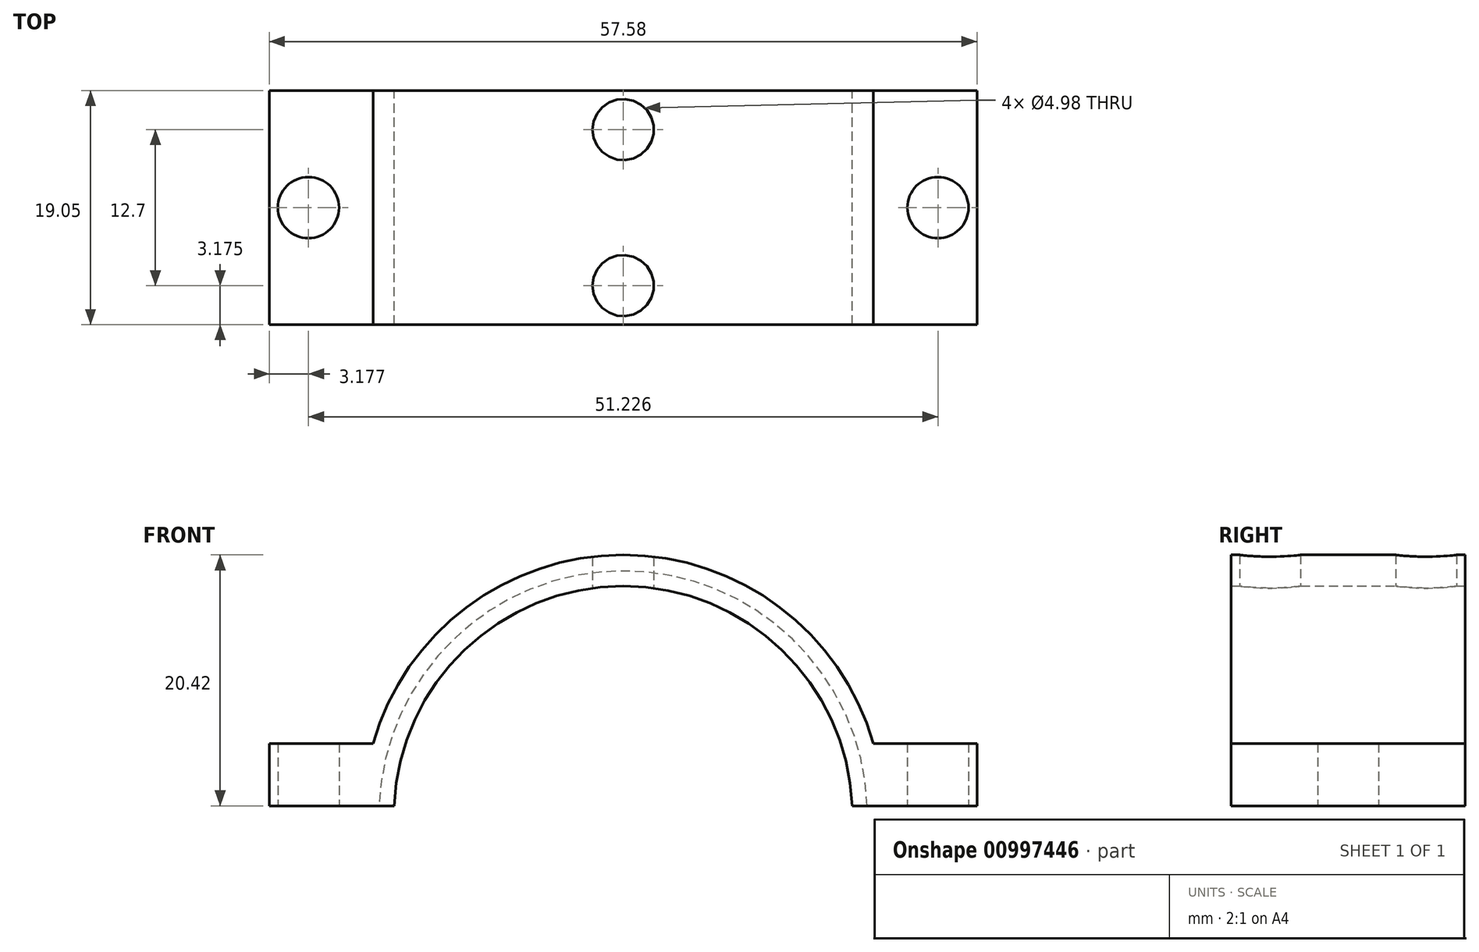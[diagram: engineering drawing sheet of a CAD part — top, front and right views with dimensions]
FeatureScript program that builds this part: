
annotation { "Feature Type Name" : "Feature", "Feature Type Description" : "" }
export const myFeature = defineFeature(function(context is Context, id is Id, definition is map)
    precondition{}
    {
        {
            var Q0;
            Q0=qCreatedBy(makeId("Front.planeOp"),FACE);
            var sketch = newSketch(context, id + "F0", { "sketchPlane" : qUnion([Q0])});
            skLineSegment(sketch, "E0", {"start": v(18.63, 0.76) * mm, "end": v(28.79, 0.76) * mm});
            skLineSegment(sketch, "E1", {"start": v(28.79, 0.76) * mm, "end": v(28.79, 5.84) * mm});
            skLineSegment(sketch, "E2", {"start": v(28.79, 5.84) * mm, "end": v(20.36, 5.84) * mm});
            skArc(sketch, "E3", {"start": v(18.63, 0.76) * mm, "mid": v(12.91, 13.45) * mm, "end": v(0, 18.64) * mm});
            skArc(sketch, "E4", {"start": v(20.36, 5.84) * mm, "mid": v(12.75, 16.92) * mm, "end": v(0, 21.18) * mm});
            skLineSegment(sketch, "E5", {"start": v(0, 21.18) * mm, "end": v(0, 18.64) * mm});
            skSolve(sketch);
        }
        {
            var Q0;
            Q0=makeQuery(id+"F0.imprint","IMPRINT",FACE,{"disambiguationData":[TD([[makeQuery(id+"F0.imprint","IMPRINT",EDGE,{"derivedFrom":sQuery(id+"F0.wireOp",EDGE,"E0")}),1.0]])]});
            extrude(context, id + "F1", {"entities" : qUnion([Q0]), "depth" : 19.05 * mm, "offsetDistance" : 25.4 * mm});
        }
        {
            var Q0;
            Q0=makeQuery(id+"F1.opExtrude","CAP_FACE",FACE,{"disambiguationData":[OSD([sQuery(id+"F0.wireOp",EDGE,"E0"),sQuery(id+"F0.wireOp",EDGE,"E1"),sQuery(id+"F0.wireOp",EDGE,"E2"),sQuery(id+"F0.wireOp",EDGE,"E3"),sQuery(id+"F0.wireOp",EDGE,"E4"),sQuery(id+"F0.wireOp",EDGE,"E5")])],"isStart":true});
            var sketch = newSketch(context, id + "F2", { "sketchPlane" : qUnion([Q0])});
            skArc(sketch, "E6", {"start": v(-19.88, 0) * mm, "mid": v(-14.05, 14.05) * mm, "end": v(0, 19.88) * mm});
            skLineSegment(sketch, "E7", {"start": v(0, 19.88) * mm, "end": v(0, 0) * mm});
            skLineSegment(sketch, "E8", {"start": v(0, 0) * mm, "end": v(-19.88, 0) * mm});
            skSolve(sketch);
        }
        {
            var Q0;
            Q0 = qSketchRegion(id + "F2", true);
            extrude(context, id + "F3", {"entities" : qUnion([Q0]), "operationType" : NewBodyOperationType.REMOVE, "oppositeDirection" : true, "depth" : 3 / 203.2 * mm, "offsetDistance" : 25.4 * mm});
        }
        {
            var Q0;
            Q0=makeQuery(id+"F1.opExtrude","SWEPT_BODY",BODY,{"disambiguationData":[OSD([sQuery(id+"F0.wireOp",EDGE,"E0"),sQuery(id+"F0.wireOp",EDGE,"E1"),sQuery(id+"F0.wireOp",EDGE,"E2"),sQuery(id+"F0.wireOp",EDGE,"E3"),sQuery(id+"F0.wireOp",EDGE,"E4"),sQuery(id+"F0.wireOp",EDGE,"E5")])]});
            var Q1;
            Q1=makeQuery(id+"F1.opExtrude","SWEPT_FACE",FACE,{"disambiguationData":[OSD([sQuery(id+"F0.wireOp",EDGE,"E5")])]});
            mirror(context, id + "F4", {"operationType" : NewBodyOperationType.ADD, "entities" : qUnion([Q0]), "mirrorPlane" : qUnion([Q1])});
        }
        {
            var Q0;
            Q0=qCreatedBy(makeId("Top.planeOp"),FACE);
            var sketch = newSketch(context, id + "F5", { "sketchPlane" : qUnion([Q0])});
            skCircle(sketch, "E9", {"center": v(0, -15.88) * mm, "radius": 2.49 * mm});
            skCircle(sketch, "E10", {"center": v(0, -3.18) * mm, "radius": 2.49 * mm});
            skLineSegment(sketch, "E11", {"start": v(-28.79, -9.53) * mm, "end": v(28.79, -9.53) * mm, "construction": true});
            skCircle(sketch, "E12", {"center": v(-25.61, -9.53) * mm, "radius": 2.49 * mm});
            skCircle(sketch, "E13", {"center": v(25.61, -9.53) * mm, "radius": 2.49 * mm});
            skLineSegment(sketch, "E14", {"start": v(0, -3.18) * mm, "end": v(0, -9.53) * mm, "construction": true});
            skLineSegment(sketch, "E15", {"start": v(0, -9.53) * mm, "end": v(0, -15.88) * mm, "construction": true});
            skSolve(sketch);
        }
        {
            var Q0;
            Q0 = qSketchRegion(id + "F5", true);
            extrude(context, id + "F6", {"entities" : qUnion([Q0]), "operationType" : NewBodyOperationType.REMOVE, "depth" : 25.4 * mm, "offsetDistance" : 25.4 * mm});
        }
    });
